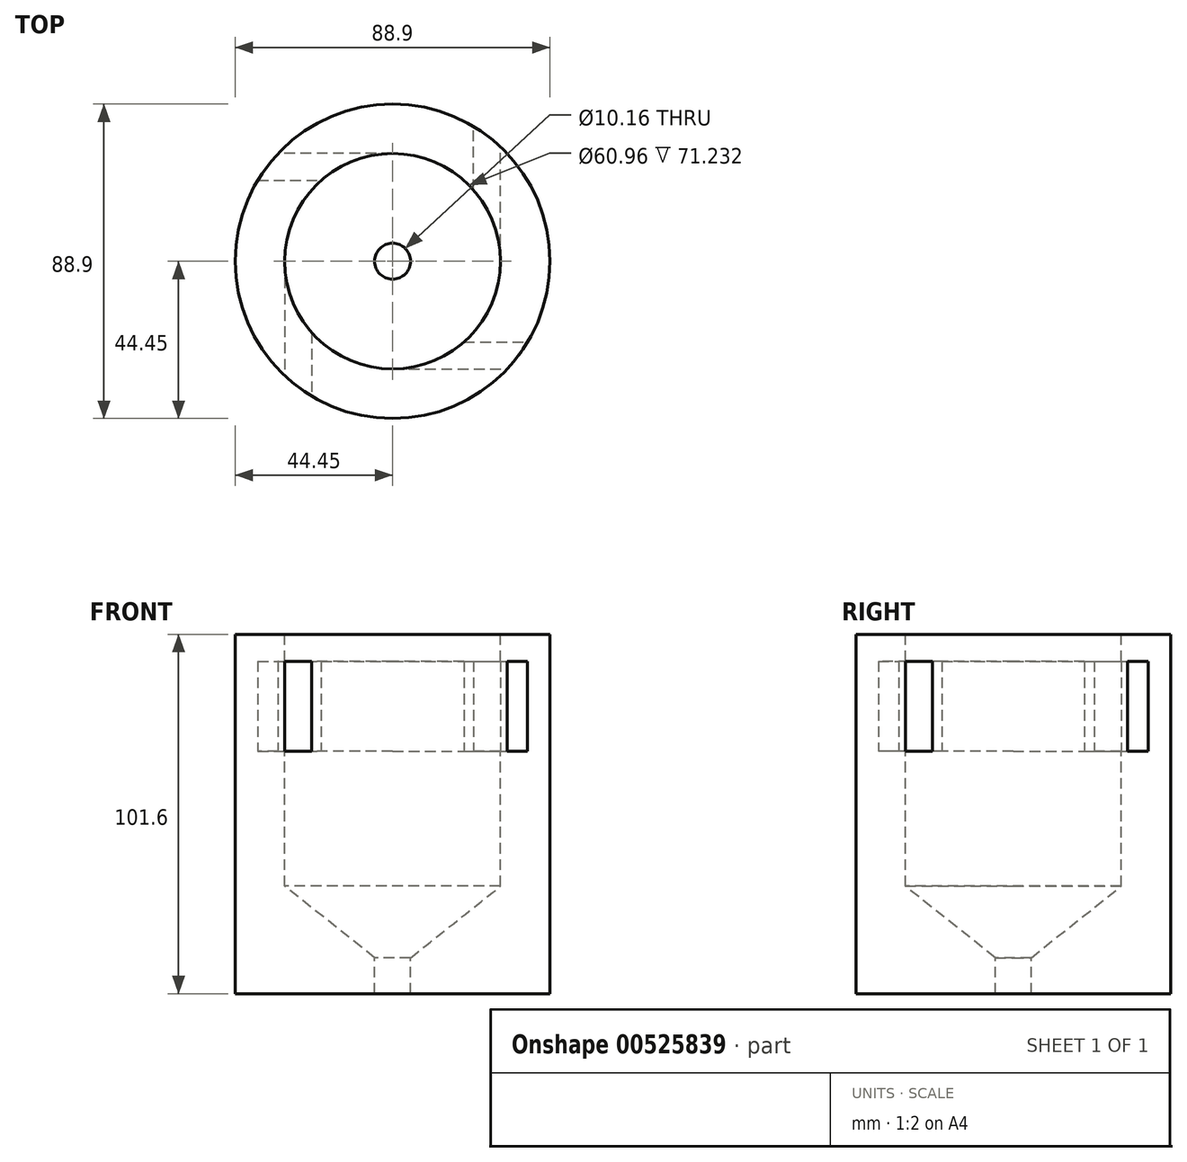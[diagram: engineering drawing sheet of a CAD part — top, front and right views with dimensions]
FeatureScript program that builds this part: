
annotation { "Feature Type Name" : "Feature", "Feature Type Description" : "" }
export const myFeature = defineFeature(function(context is Context, id is Id, definition is map)
    precondition{}
    {
        {
            var Q0;
            Q0=qCreatedBy(makeId("Front.planeOp"),FACE);
            var sketch = newSketch(context, id + "F0", { "sketchPlane" : qUnion([Q0])});
            skLineSegment(sketch, "E0", {"start": v(5.08, -20.32) * mm, "end": v(5.08, -30.48) * mm});
            skLineSegment(sketch, "E1", {"start": v(5.08, -30.48) * mm, "end": v(44.45, -30.48) * mm});
            skLineSegment(sketch, "E2", {"start": v(44.45, -30.48) * mm, "end": v(44.45, 38.1) * mm});
            skLineSegment(sketch, "E3", {"start": v(44.45, 38.1) * mm, "end": v(30.48, 38.1) * mm});
            skLineSegment(sketch, "E4", {"start": v(30.48, 38.1) * mm, "end": v(30.48, -0.11) * mm});
            skLineSegment(sketch, "E5", {"start": v(30.48, -0.11) * mm, "end": v(5.08, -20.32) * mm});
            skLineSegment(sketch, "E6", {"start": v(0, 50.8) * mm, "end": v(0, 0) * mm});
            skSolve(sketch);
        }
        {
            var Q0;
            Q0 = qSketchRegion(id + "F0", true);
            var Q1;
            Q1=sQuery(id+"F0.wireOp",EDGE,"E6");
            revolve(context, id + "F1", {"entities" : qUnion([Q0]), "axis" : qUnion([Q1]), "revolveType" : RevolveType.ONE_DIRECTION, "angle" : 360 * degree});
        }
        {
            var Q0;
            Q0=makeQuery(id+"F1.opRevolve","SWEPT_FACE",FACE,{"disambiguationData":[OSD([sQuery(id+"F0.wireOp",EDGE,"E3")])]});
            var sketch = newSketch(context, id + "F2", { "sketchPlane" : qUnion([Q0])});
            skLineSegment(sketch, "E7", {"start": v(30.48, 0) * mm, "end": v(30.48, 32.35) * mm});
            skLineSegment(sketch, "E8", {"start": v(22.86, 20.16) * mm, "end": v(22.86, 38.12) * mm});
            skLineSegment(sketch, "E9", {"start": v(0, 30.48) * mm, "end": v(-32.35, 30.48) * mm});
            skLineSegment(sketch, "E10", {"start": v(-38.12, 22.86) * mm, "end": v(-20.16, 22.86) * mm});
            skLineSegment(sketch, "E11", {"start": v(-30.48, 0) * mm, "end": v(-30.48, -32.35) * mm});
            skLineSegment(sketch, "E12", {"start": v(-22.86, -20.16) * mm, "end": v(-22.86, -38.12) * mm});
            skLineSegment(sketch, "E13", {"start": v(0, -30.48) * mm, "end": v(32.35, -30.48) * mm});
            skLineSegment(sketch, "E14", {"start": v(20.16, -22.86) * mm, "end": v(38.12, -22.86) * mm});
            skArc(sketch, "E15", {"start": v(22.86, 38.12) * mm, "mid": v(-6.1, 44.03) * mm, "end": v(-32.35, 30.48) * mm});
            skArc(sketch, "E16", {"start": v(-38.12, 22.86) * mm, "mid": v(-44.03, -6.1) * mm, "end": v(-30.48, -32.35) * mm});
            skArc(sketch, "E17", {"start": v(-22.86, -38.12) * mm, "mid": v(6.1, -44.03) * mm, "end": v(32.35, -30.48) * mm});
            skArc(sketch, "E18", {"start": v(30.48, 32.35) * mm, "mid": v(44.03, 6.1) * mm, "end": v(38.12, -22.86) * mm});
            skArc(sketch, "E19", {"start": v(0, 30.48) * mm, "mid": v(12.54, 27.78) * mm, "end": v(22.86, 20.16) * mm});
            skArc(sketch, "E20", {"start": v(30.48, 0) * mm, "mid": v(27.78, -12.54) * mm, "end": v(20.16, -22.86) * mm});
            skArc(sketch, "E21", {"start": v(-20.16, 22.86) * mm, "mid": v(-27.78, 12.54) * mm, "end": v(-30.48, 0) * mm});
            skArc(sketch, "E22", {"start": v(-22.86, -20.16) * mm, "mid": v(-12.54, -27.78) * mm, "end": v(0, -30.48) * mm});
            skSolve(sketch);
        }
        {
            var Q0;
            Q0=makeQuery(id+"F2.imprint","IMPRINT",FACE,{"disambiguationData":[TD([[makeQuery(id+"F2.imprint","IMPRINT",EDGE,{"derivedFrom":sQuery(id+"F2.wireOp",EDGE,"E8")}),1.0]])]});
            var Q1;
            Q1=makeQuery(id+"F2.imprint","IMPRINT",FACE,{"disambiguationData":[TD([[makeQuery(id+"F2.imprint","IMPRINT",EDGE,{"derivedFrom":sQuery(id+"F2.wireOp",EDGE,"E7")}),-1.0]])]});
            var Q2;
            Q2=makeQuery(id+"F2.imprint","IMPRINT",FACE,{"disambiguationData":[TD([[makeQuery(id+"F2.imprint","IMPRINT",EDGE,{"derivedFrom":sQuery(id+"F2.wireOp",EDGE,"E12")}),1.0]])]});
            var Q3;
            Q3=makeQuery(id+"F2.imprint","IMPRINT",FACE,{"disambiguationData":[TD([[makeQuery(id+"F2.imprint","IMPRINT",EDGE,{"derivedFrom":sQuery(id+"F2.wireOp",EDGE,"E10")}),-1.0]])]});
            extrude(context, id + "F3", {"entities" : qUnion([Q0, Q1, Q2, Q3]), "operationType" : NewBodyOperationType.ADD, "depth" : 25.4 * mm, "offsetDistance" : 25.4 * mm});
        }
        {
            var Q0;
            Q0=qCreatedBy(makeId("Front.planeOp"),FACE);
            var sketch = newSketch(context, id + "F4", { "sketchPlane" : qUnion([Q0])});
            skLineSegment(sketch, "E23", {"start": v(44.45, 63.5) * mm, "end": v(44.45, 71.12) * mm});
            skLineSegment(sketch, "E24", {"start": v(44.45, 63.5) * mm, "end": v(44.45, -33.41) * mm});
            skLineSegment(sketch, "E25", {"start": v(44.45, 71.12) * mm, "end": v(30.48, 71.12) * mm});
            skLineSegment(sketch, "E26", {"start": v(30.48, 71.12) * mm, "end": v(30.48, 63.5) * mm});
            skLineSegment(sketch, "E27", {"start": v(30.48, 63.5) * mm, "end": v(44.45, 63.5) * mm});
            skLineSegment(sketch, "E28", {"start": v(0, 0) * mm, "end": v(0, 77.57) * mm});
            skLineSegment(sketch, "E29", {"start": v(0, 0) * mm, "end": v(61.78, 0) * mm});
            skSolve(sketch);
        }
        {
            var Q0;
            Q0=makeQuery(id+"F4.imprint","IMPRINT",FACE,{"disambiguationData":[TD([[makeQuery(id+"F4.imprint","IMPRINT",EDGE,{"derivedFrom":sQuery(id+"F4.wireOp",EDGE,"E23")}),1.0]])]});
            var Q1;
            Q1=sQuery(id+"F4.wireOp",EDGE,"E28");
            revolve(context, id + "F5", {"operationType" : NewBodyOperationType.ADD, "entities" : qUnion([Q0]), "axis" : qUnion([Q1]), "revolveType" : RevolveType.FULL});
        }
    });
